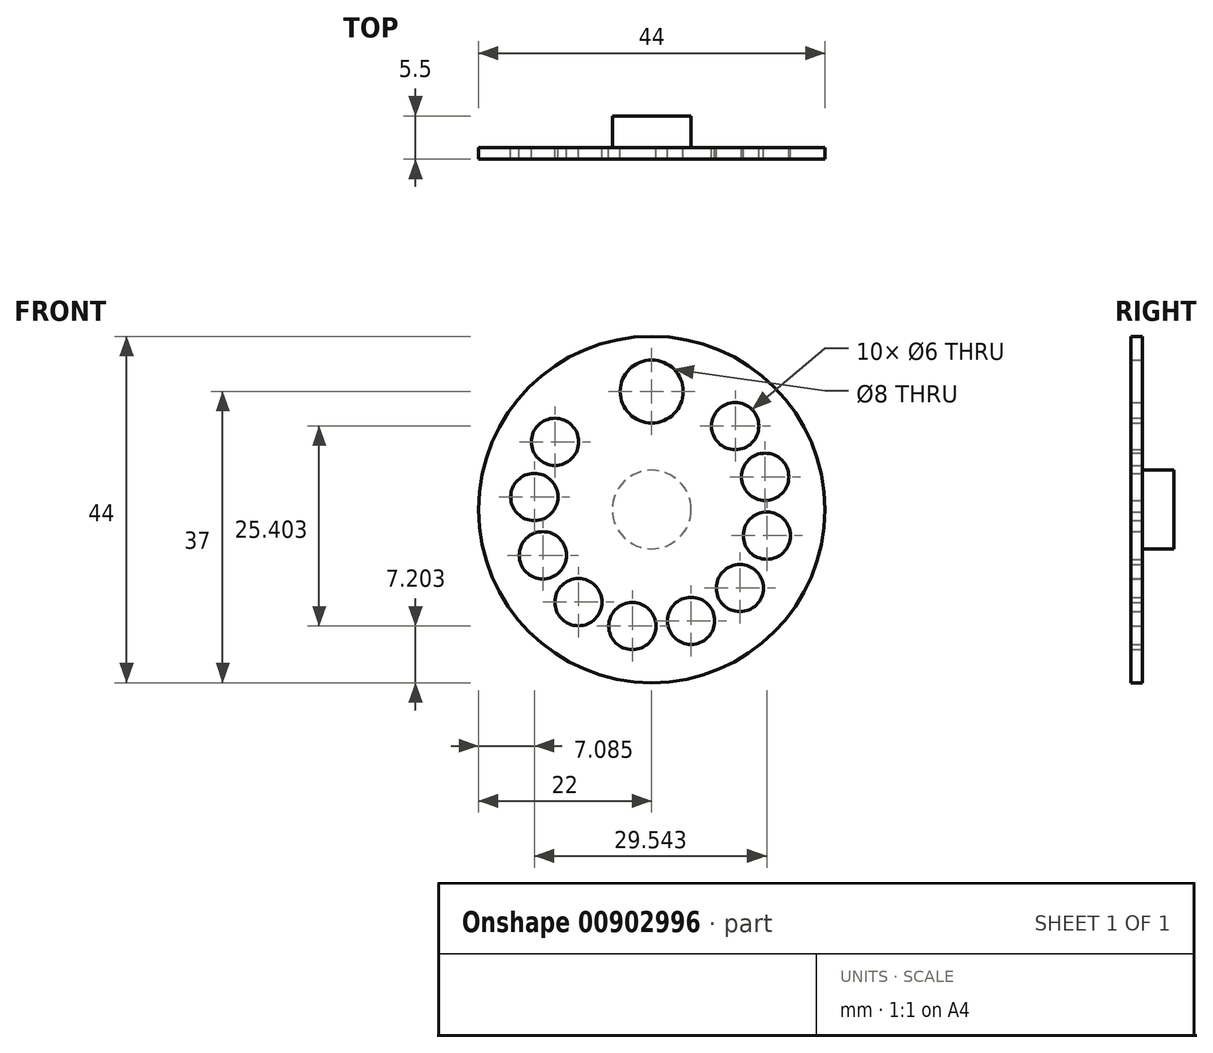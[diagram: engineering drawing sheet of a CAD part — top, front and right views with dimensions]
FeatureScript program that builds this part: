
annotation { "Feature Type Name" : "Feature", "Feature Type Description" : "" }
export const myFeature = defineFeature(function(context is Context, id is Id, definition is map)
    precondition{}
    {
        {
            var Q0;
            Q0=qCreatedBy(makeId("Front.planeOp"),FACE);
            var sketch = newSketch(context, id + "F0", { "sketchPlane" : qUnion([Q0])});
            skLineSegment(sketch, "E0", {"start": v(0, 0) * mm, "end": v(0, 15) * mm, "construction": true});
            skLineSegment(sketch, "E1", {"start": v(0, 15) * mm, "end": v(10.6, 10.6) * mm, "construction": true});
            skLineSegment(sketch, "E2", {"start": v(10.6, 10.6) * mm, "end": v(0, 0) * mm, "construction": true});
            skCircle(sketch, "E3", {"center": v(0, 0) * mm, "radius": 22 * mm});
            skCircle(sketch, "E4", {"center": v(0, 15) * mm, "radius": 4 * mm});
            skCircle(sketch, "E5", {"center": v(10.6, 10.6) * mm, "radius": 3 * mm});
            skCircle(sketch, "E6.1.0", {"center": v(14.41, 4.16) * mm, "radius": 3 * mm});
            skCircle(sketch, "E6.2.0", {"center": v(14.63, -3.32) * mm, "radius": 3 * mm});
            skLineSegment(sketch, "E6.anchor1", {"start": v(0, 0) * mm, "end": v(10.6, 10.6) * mm, "construction": true});
            skLineSegment(sketch, "E6.anchor2", {"start": v(0, 0) * mm, "end": v(-12.29, 8.6) * mm, "construction": true});
            skCircle(sketch, "E7.1.3.0", {"center": v(11.2, -9.97) * mm, "radius": 3 * mm});
            skCircle(sketch, "E7.1.4.0", {"center": v(5, -14.14) * mm, "radius": 3 * mm});
            skCircle(sketch, "E7.1.5.0", {"center": v(-2.46, -14.8) * mm, "radius": 3 * mm});
            skCircle(sketch, "E7.1.6.0", {"center": v(-9.3, -11.77) * mm, "radius": 3 * mm});
            skCircle(sketch, "E7.1.7.0", {"center": v(-13.83, -5.8) * mm, "radius": 3 * mm});
            skCircle(sketch, "E7.1.8.0", {"center": v(-14.91, 1.6) * mm, "radius": 3 * mm});
            skCircle(sketch, "E7.1.9.0", {"center": v(-12.29, 8.6) * mm, "radius": 3 * mm});
            skSolve(sketch);
        }
        {
            var Q0;
            Q0 = qSketchRegion(id + "F0", true);
            extrude(context, id + "F1", {"entities" : qUnion([Q0]), "depth" : 1.5 * mm, "offsetDistance" : 25 * mm});
        }
        {
            var Q0;
            Q0=makeQuery(id+"F1.opExtrude","CAP_FACE",FACE,{"disambiguationData":[OSD([sQuery(id+"F0.wireOp",EDGE,"E3"),sQuery(id+"F0.wireOp",EDGE,"E4"),sQuery(id+"F0.wireOp",EDGE,"E5"),sQuery(id+"F0.wireOp",EDGE,"E6.1.0"),sQuery(id+"F0.wireOp",EDGE,"E6.2.0"),sQuery(id+"F0.wireOp",EDGE,"E7.1.3.0"),sQuery(id+"F0.wireOp",EDGE,"E7.1.4.0"),sQuery(id+"F0.wireOp",EDGE,"E7.1.5.0"),sQuery(id+"F0.wireOp",EDGE,"E7.1.6.0"),sQuery(id+"F0.wireOp",EDGE,"E7.1.7.0"),sQuery(id+"F0.wireOp",EDGE,"E7.1.8.0"),sQuery(id+"F0.wireOp",EDGE,"E7.1.9.0")])],"isStart":true});
            var sketch = newSketch(context, id + "F2", { "sketchPlane" : qUnion([Q0])});
            skCircle(sketch, "E8", {"center": v(0, 0) * mm, "radius": 5 * mm});
            skSolve(sketch);
        }
        {
            var Q0;
            Q0 = qSketchRegion(id + "F2", true);
            extrude(context, id + "F3", {"entities" : qUnion([Q0]), "operationType" : NewBodyOperationType.ADD, "depth" : 4 * mm, "offsetDistance" : 25 * mm});
        }
    });
